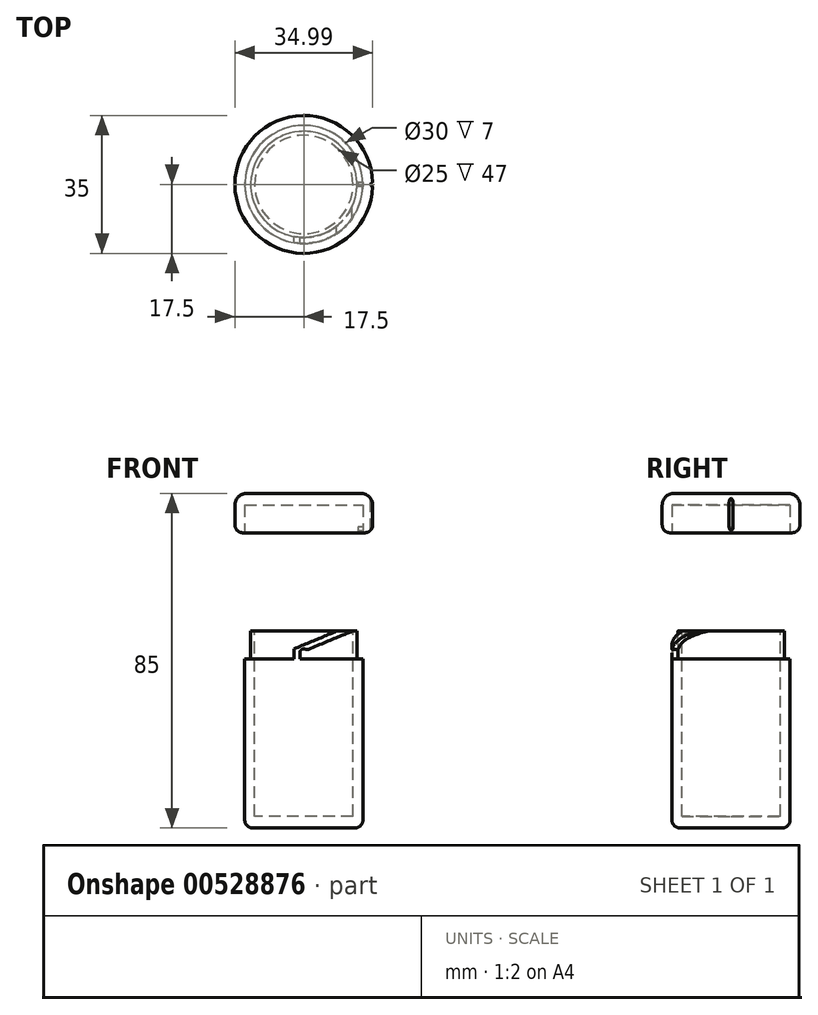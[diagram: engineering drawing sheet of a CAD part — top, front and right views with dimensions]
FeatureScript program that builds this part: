
annotation { "Feature Type Name" : "Feature", "Feature Type Description" : "" }
export const myFeature = defineFeature(function(context is Context, id is Id, definition is map)
    precondition{}
    {
        {
            var Q0;
            Q0=qCreatedBy(makeId("Top.planeOp"),FACE);
            var sketch = newSketch(context, id + "F0", { "sketchPlane" : qUnion([Q0])});
            skCircle(sketch, "E0", {"center": v(0, 0) * mm, "radius": 15 * mm});
            skSolve(sketch);
        }
        {
            var Q0;
            Q0 = qSketchRegion(id + "F0", true);
            extrude(context, id + "F1", {"entities" : qUnion([Q0]), "depth" : 50 * mm, "offsetDistance" : 25 * mm});
        }
        {
            var Q0;
            Q0=makeQuery(id+"F1.opExtrude","CAP_EDGE",EDGE,{"disambiguationData":[OSD([sQuery(id+"F0.wireOp",EDGE,"E0")])],"isStart":true});
            fillet(context, id + "F2", {"entities" : qUnion([Q0]), "radius" : 2 * mm, "tangentPropagation" : true, "allowEdgeOverflow" : false});
        }
        {
            var Q0;
            Q0=makeQuery(id+"F1.opExtrude","CAP_FACE",FACE,{"disambiguationData":[OSD([sQuery(id+"F0.wireOp",EDGE,"E0")])],"isStart":false});
            var sketch = newSketch(context, id + "F3", { "sketchPlane" : qUnion([Q0])});
            skCircle(sketch, "E1", {"center": v(0, 0) * mm, "radius": 16.5 * mm});
            skCircle(sketch, "E2", {"center": v(0, 0) * mm, "radius": 13.5 * mm});
            skSolve(sketch);
        }
        {
            var Q0;
            Q0 = qSketchRegion(id + "F3", true);
            extrude(context, id + "F4", {"entities" : qUnion([Q0]), "operationType" : NewBodyOperationType.REMOVE, "oppositeDirection" : true, "depth" : 7 * mm, "offsetDistance" : 25 * mm});
        }
        {
            var Q0;
            Q0=qCreatedBy(makeId("Front.planeOp"),FACE);
            var sketch = newSketch(context, id + "F5", { "sketchPlane" : qUnion([Q0])});
            skLineSegment(sketch, "E3", {"start": v(12.28, 50) * mm, "end": v(1.2, 45.4) * mm});
            skLineSegment(sketch, "E4", {"start": v(8.36, 50) * mm, "end": v(-2.5, 45.5) * mm});
            skLineSegment(sketch, "E5", {"start": v(-2.5, 45.5) * mm, "end": v(-2.5, 43) * mm});
            skLineSegment(sketch, "E6", {"start": v(-2.5, 43) * mm, "end": v(-1, 43) * mm});
            skLineSegment(sketch, "E7", {"start": v(-1, 43) * mm, "end": v(-1, 44.5) * mm});
            skArc(sketch, "E8", {"start": v(-1, 44.5) * mm, "mid": v(-0.55, 45.34) * mm, "end": v(0.4, 45.41) * mm});
            skArc(sketch, "E9", {"start": v(0.4, 45.41) * mm, "mid": v(0.8, 45.33) * mm, "end": v(1.2, 45.4) * mm});
            skLineSegment(sketch, "E10", {"start": v(8.36, 50) * mm, "end": v(12.28, 50) * mm});
            skSolve(sketch);
        }
        {
            var Q0;
            Q0 = qSketchRegion(id + "F5", true);
            extrude(context, id + "F6", {"entities" : qUnion([Q0]), "operationType" : NewBodyOperationType.ADD, "depth" : 16 * mm, "offsetDistance" : 25 * mm});
        }
        {
            var Q0;
            Q0=qCreatedBy(makeId("Front.planeOp"),FACE);
            var sketch = newSketch(context, id + "F7", { "sketchPlane" : qUnion([Q0])});
            skLineSegment(sketch, "E11", {"start": v(0, 58) * mm, "end": v(0, 34.14) * mm, "construction": true});
            skSolve(sketch);
        }
        {
            var Q0;
            Q0=makeQuery(id+"F6.boolean.opBoolean","MERGE",FACE,{"derivedFrom":[makeQuery(id+"F1.opExtrude","CAP_FACE",FACE,{"disambiguationData":[OSD([sQuery(id+"F0.wireOp",EDGE,"E0")])],"isStart":false}),makeQuery(id+"F6.opExtrude","SWEPT_FACE",FACE,{"disambiguationData":[OSD([sQuery(id+"F5.wireOp",EDGE,"3otQBRoi-I1nU-lV5x-rrkb-oaM1KIzqOUw1")])]})]});
            var sketch = newSketch(context, id + "F8", { "sketchPlane" : qUnion([Q0])});
            skCircle(sketch, "E12", {"center": v(0, 0) * mm, "radius": 22.5 * mm});
            skCircle(sketch, "E13", {"center": v(0, 0) * mm, "radius": 15 * mm});
            skSolve(sketch);
        }
        {
            var Q0;
            Q0 = qSketchRegion(id + "F8", true);
            extrude(context, id + "F9", {"entities" : qUnion([Q0]), "operationType" : NewBodyOperationType.REMOVE, "oppositeDirection" : true, "depth" : 7 * mm, "offsetDistance" : 25 * mm});
        }
        {
            var Q0;
            {var subQ0=sQuery(id+"F5.wireOp",EDGE,"E10");Q0=makeQuery(id+"FHVM9mGuFrvkW5w_1.2.F6.boolean.opBoolean","MERGE",FACE,{"derivedFrom":[makeQuery(id+"FHVM9mGuFrvkW5w_1.1.F6.boolean.opBoolean","MERGE",FACE,{"derivedFrom":[makeQuery(id+"F6.boolean.opBoolean","MERGE",FACE,{"derivedFrom":[makeQuery(id+"F1.opExtrude","CAP_FACE",FACE,{"disambiguationData":[OSD([sQuery(id+"F0.wireOp",EDGE,"E0")])],"isStart":false}),makeQuery(id+"F6.opExtrude","SWEPT_FACE",FACE,{"disambiguationData":[OSD([subQ0])]})]}),makeQuery(id+"FHVM9mGuFrvkW5w_1.1.F6.opExtrude","SWEPT_FACE",FACE,{"disambiguationData":[OSD([subQ0])]})]}),makeQuery(id+"FHVM9mGuFrvkW5w_1.2.F6.opExtrude","SWEPT_FACE",FACE,{"disambiguationData":[OSD([subQ0])]})]});}
            cPlane(context, id + "F10", {"entities" : qUnion([Q0]), "cplaneType" : CPlaneType.OFFSET, "offset" : 25 * mm, "width" : 150 * mm, "height" : 150 * mm});
        }
        {
            var Q0;
            Q0=qCreatedBy(id+"F10.planeOp",FACE);
            var sketch = newSketch(context, id + "F11", { "sketchPlane" : qUnion([Q0])});
            skCircle(sketch, "E14", {"center": v(0, 0) * mm, "radius": 17.5 * mm});
            skSolve(sketch);
        }
        {
            var Q0;
            Q0 = qSketchRegion(id + "F11", true);
            extrude(context, id + "F12", {"entities" : qUnion([Q0]), "depth" : 10 * mm, "offsetDistance" : 25 * mm});
        }
        {
            var Q0;
            Q0=makeQuery(id+"F12.opExtrude","CAP_EDGE",EDGE,{"disambiguationData":[OSD([sQuery(id+"F11.wireOp",EDGE,"E14")])],"isStart":false});
            fillet(context, id + "F13", {"entities" : qUnion([Q0]), "radius" : 3 * mm, "tangentPropagation" : true, "allowEdgeOverflow" : false});
        }
        {
            var Q0;
            Q0=makeQuery(id+"F12.opExtrude","CAP_EDGE",EDGE,{"disambiguationData":[OSD([sQuery(id+"F11.wireOp",EDGE,"E14")])],"isStart":true});
            fillet(context, id + "F14", {"entities" : qUnion([Q0]), "radius" : 2 * mm, "tangentPropagation" : true, "allowEdgeOverflow" : false});
        }
        {
            var Q0;
            Q0=makeQuery(id+"F12.opExtrude","CAP_FACE",FACE,{"disambiguationData":[OSD([sQuery(id+"F11.wireOp",EDGE,"E14")])],"isStart":false});
            var sketch = newSketch(context, id + "F15", { "sketchPlane" : qUnion([Q0])});
            skCircle(sketch, "E15", {"center": v(17.5, 0) * mm, "radius": 0.5 * mm});
            skSolve(sketch);
        }
        {
            var Q0;
            Q0 = qSketchRegion(id + "F15", true);
            extrude(context, id + "F16", {"entities" : qUnion([Q0]), "operationType" : NewBodyOperationType.REMOVE, "oppositeDirection" : true, "depth" : 10 * mm, "offsetDistance" : 25 * mm});
        }
        {
            var Q0;
            Q0=makeQuery(id+"F12.opExtrude","CAP_FACE",FACE,{"disambiguationData":[OSD([sQuery(id+"F11.wireOp",EDGE,"E14")])],"isStart":true});
            var sketch = newSketch(context, id + "F17", { "sketchPlane" : qUnion([Q0])});
            skCircle(sketch, "E16", {"center": v(0, 0) * mm, "radius": 15 * mm});
            skSolve(sketch);
        }
        {
            var Q0;
            Q0 = qSketchRegion(id + "F17", true);
            extrude(context, id + "F18", {"entities" : qUnion([Q0]), "operationType" : NewBodyOperationType.REMOVE, "oppositeDirection" : true, "depth" : 7 * mm, "offsetDistance" : 25 * mm});
        }
        {
            var Q0;
            Q0=qCreatedBy(makeId("Right.planeOp"),FACE);
            var sketch = newSketch(context, id + "F19", { "sketchPlane" : qUnion([Q0])});
            skCircle(sketch, "E17", {"center": v(0, 76) * mm, "radius": 0.5 * mm});
            skSolve(sketch);
        }
        {
            var Q0;
            Q0 = qSketchRegion(id + "F19", true);
            extrude(context, id + "F20", {"entities" : qUnion([Q0]), "operationType" : NewBodyOperationType.ADD, "depth" : 16 * mm, "offsetDistance" : 25 * mm});
        }
        {
            var Q0;
            Q0=makeQuery(id+"F12.opExtrude","CAP_FACE",FACE,{"disambiguationData":[OSD([sQuery(id+"F11.wireOp",EDGE,"E14")])],"isStart":true});
            var sketch = newSketch(context, id + "F21", { "sketchPlane" : qUnion([Q0])});
            skCircle(sketch, "E18", {"center": v(0, 0) * mm, "radius": 13.75 * mm});
            skSolve(sketch);
        }
        {
            var Q0;
            Q0=makeQuery(id+"F21.imprint","IMPRINT",FACE,{"disambiguationData":[TD([[makeQuery(id+"F21.imprint","IMPRINT",EDGE,{"derivedFrom":sQuery(id+"F21.wireOp",EDGE,"E18")}),1.0]])]});
            var sketch = newSketch(context, id + "F22", { "sketchPlane" : qUnion([Q0])});
            skCircle(sketch, "E19", {"center": v(0, 0) * mm, "radius": 13.75 * mm});
            skSolve(sketch);
        }
        {
            var Q0;
            Q0 = qSketchRegion(id + "F22", true);
            extrude(context, id + "F23", {"entities" : qUnion([Q0]), "operationType" : NewBodyOperationType.REMOVE, "oppositeDirection" : true, "depth" : 7 * mm, "offsetDistance" : 25 * mm});
        }
        {
            var Q0;
            {var subQ0=sQuery(id+"F5.wireOp",EDGE,"E10");Q0=makeQuery(id+"FHVM9mGuFrvkW5w_1.2.F6.boolean.opBoolean","MERGE",FACE,{"derivedFrom":[makeQuery(id+"FHVM9mGuFrvkW5w_1.1.F6.boolean.opBoolean","MERGE",FACE,{"derivedFrom":[makeQuery(id+"F6.boolean.opBoolean","MERGE",FACE,{"derivedFrom":[makeQuery(id+"F1.opExtrude","CAP_FACE",FACE,{"disambiguationData":[OSD([sQuery(id+"F0.wireOp",EDGE,"E0")])],"isStart":false}),makeQuery(id+"F6.opExtrude","SWEPT_FACE",FACE,{"disambiguationData":[OSD([subQ0])]})]}),makeQuery(id+"FHVM9mGuFrvkW5w_1.1.F6.opExtrude","SWEPT_FACE",FACE,{"disambiguationData":[OSD([subQ0])]})]}),makeQuery(id+"FHVM9mGuFrvkW5w_1.2.F6.opExtrude","SWEPT_FACE",FACE,{"disambiguationData":[OSD([subQ0])]})]});}
            var sketch = newSketch(context, id + "F24", { "sketchPlane" : qUnion([Q0])});
            skCircle(sketch, "E20", {"center": v(0, 0) * mm, "radius": 12.5 * mm});
            skSolve(sketch);
        }
        {
            var Q0;
            Q0 = qSketchRegion(id + "F24", true);
            extrude(context, id + "F25", {"entities" : qUnion([Q0]), "operationType" : NewBodyOperationType.REMOVE, "oppositeDirection" : true, "depth" : 47 * mm, "offsetDistance" : 25 * mm});
        }
    });
